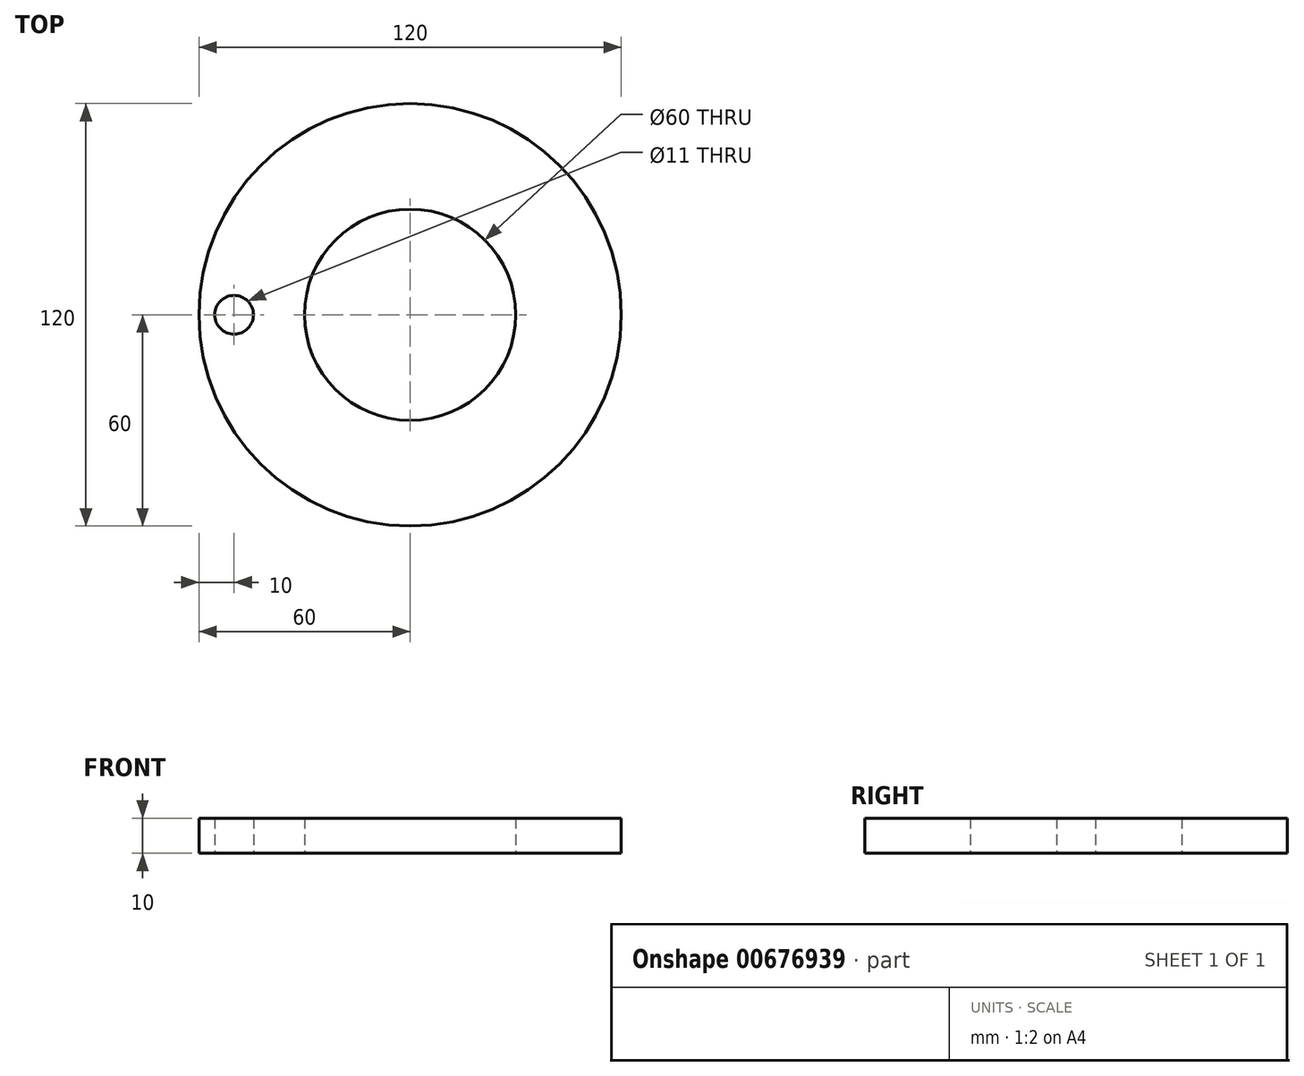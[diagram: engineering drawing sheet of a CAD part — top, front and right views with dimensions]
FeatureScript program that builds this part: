
annotation { "Feature Type Name" : "Feature", "Feature Type Description" : "" }
export const myFeature = defineFeature(function(context is Context, id is Id, definition is map)
    precondition{}
    {
        {
            var Q0;
            Q0=qCreatedBy(makeId("Top.planeOp"),FACE);
            var sketch = newSketch(context, id + "F0", { "sketchPlane" : qUnion([Q0])});
            skCircle(sketch, "E0", {"center": v(0, 0) * mm, "radius": 30 * mm});
            skCircle(sketch, "E1", {"center": v(0, 0) * mm, "radius": 60 * mm});
            skSolve(sketch);
        }
        {
            var Q0;
            Q0=makeQuery(id+"F0.imprint","IMPRINT",FACE,{"disambiguationData":[TD([[makeQuery(id+"F0.imprint","IMPRINT",EDGE,{"derivedFrom":sQuery(id+"F0.wireOp",EDGE,"E0")}),-1.0]])]});
            extrude(context, id + "F1", {"entities" : qUnion([Q0]), "depth" : 10 * mm, "offsetDistance" : 25 * mm});
        }
        {
            var Q0;
            Q0=makeQuery(id+"F1.opExtrude","CAP_FACE",FACE,{"disambiguationData":[OSD([sQuery(id+"F0.wireOp",EDGE,"E0"),sQuery(id+"F0.wireOp",EDGE,"E1")])],"isStart":false});
            var sketch = newSketch(context, id + "F2", { "sketchPlane" : qUnion([Q0])});
            skPoint(sketch, "E2", {"position": v(-50, 0) * mm});
            skSolve(sketch);
        }
        {
            var Q0;
            Q0=sQuery(id+"F2.wireOp",VERTEX,"E2");
            var Q1;
            Q1=makeQuery(id+"F1.opExtrude","SWEPT_BODY",BODY,{"disambiguationData":[OSD([sQuery(id+"F0.wireOp",EDGE,"E0"),sQuery(id+"F0.wireOp",EDGE,"E1")])]});
            hole(context, id + "F3", {"style" : HoleStyle.SIMPLE, "endStyle" : HoleEndStyle.THROUGH, "holeDiameter" : 11 * mm, "majorDiameter" : 5 * mm, "isTappedThrough" : true, "tappedDepth" : 12 * mm, "tapClearance" : 3, "locations" : qUnion([Q0]), "scope" : qUnion([Q1])});
        }
    });
